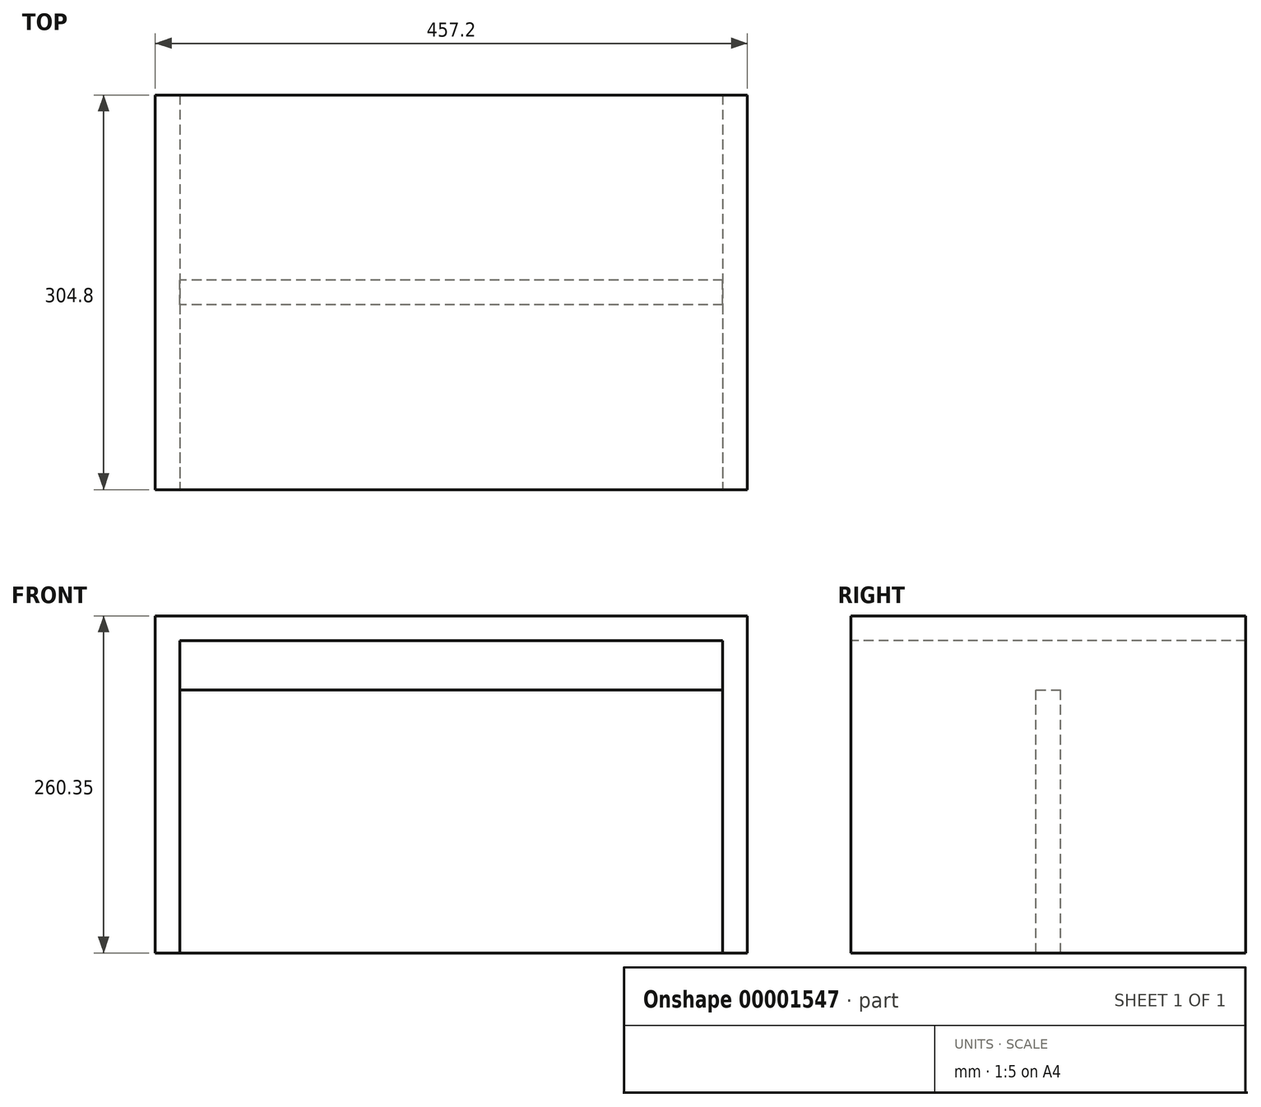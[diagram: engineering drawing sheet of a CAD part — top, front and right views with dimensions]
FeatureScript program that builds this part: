
annotation { "Feature Type Name" : "Feature", "Feature Type Description" : "" }
export const myFeature = defineFeature(function(context is Context, id is Id, definition is map)
    precondition{}
    {
        {
            var Q0;
            Q0=qCreatedBy(makeId("Top.planeOp"),FACE);
            var sketch = newSketch(context, id + "F0", { "sketchPlane" : qUnion([Q0])});
            skLineSegment(sketch, "E0.bottom", {"start": v(-228.6, 152.4) * mm, "end": v(228.6, 152.4) * mm});
            skLineSegment(sketch, "E0.top", {"start": v(-228.6, -152.4) * mm, "end": v(228.6, -152.4) * mm});
            skLineSegment(sketch, "E0.left", {"start": v(-228.6, 152.4) * mm, "end": v(-228.6, -152.4) * mm});
            skLineSegment(sketch, "E0.right", {"start": v(228.6, 152.4) * mm, "end": v(228.6, -152.4) * mm});
            skSolve(sketch);
        }
        {
            var Q0;
            Q0=makeQuery(id+"F0.imprint","IMPRINT",FACE,{"disambiguationData":[TD([[makeQuery(id+"F0.imprint","IMPRINT",EDGE,{"derivedFrom":sQuery(id+"F0.wireOp",EDGE,"E0.bottom")}),-1.0]])]});
            extrude(context, id + "F1", {"entities" : qUnion([Q0]), "depth" : 260.35 * mm});
        }
        {
            var Q0;
            Q0=makeQuery(id+"F1.opExtrude","SWEPT_FACE",FACE,{"disambiguationData":[OSD([sQuery(id+"F0.wireOp",EDGE,"E0.bottom")])]});
            var Q1;
            Q1=makeQuery(id+"F1.opExtrude","SWEPT_FACE",FACE,{"disambiguationData":[OSD([sQuery(id+"F0.wireOp",EDGE,"E0.top")])]});
            var Q2;
            Q2=makeQuery(id+"F1.opExtrude","CAP_FACE",FACE,{"disambiguationData":[OSD([sQuery(id+"F0.wireOp",EDGE,"E0.bottom"),sQuery(id+"F0.wireOp",EDGE,"E0.top"),sQuery(id+"F0.wireOp",EDGE,"E0.left"),sQuery(id+"F0.wireOp",EDGE,"E0.right")])],"isStart":true});
            shell(context, id + "F2", {"entities" : qUnion([Q0, Q1, Q2]), "thickness" : 19.05 * mm});
        }
        {
            var Q0;
            Q0=qCreatedBy(makeId("Front.planeOp"),FACE);
            var sketch = newSketch(context, id + "F3", { "sketchPlane" : qUnion([Q0])});
            skLineSegment(sketch, "E1.left", {"start": v(209.55, 0) * mm, "end": v(209.55, 0) * mm});
            skLineSegment(sketch, "E1.right", {"start": v(-208.76, 0) * mm, "end": v(-208.76, 0) * mm});
            skLineSegment(sketch, "E2.bottom", {"start": v(209.55, 0) * mm, "end": v(-209.55, 0) * mm});
            skLineSegment(sketch, "E2.top", {"start": v(209.55, 203.2) * mm, "end": v(-209.55, 203.2) * mm});
            skLineSegment(sketch, "E2.left", {"start": v(209.55, 0) * mm, "end": v(209.55, 203.2) * mm});
            skLineSegment(sketch, "E2.right", {"start": v(-209.55, 0) * mm, "end": v(-209.55, 203.2) * mm});
            skLineSegment(sketch, "E3.0", {"start": v(209.55, 241.3) * mm, "end": v(209.55, 0) * mm, "construction": true});
            skSolve(sketch);
        }
        {
            var Q0;
            Q0 = qSketchRegion(id + "F3", true);
            extrude(context, id + "F4", {"entities" : qUnion([Q0]), "operationType" : NewBodyOperationType.ADD, "endBound" : BoundingType.SYMMETRIC, "depth" : 19.05 * mm});
        }
    });
